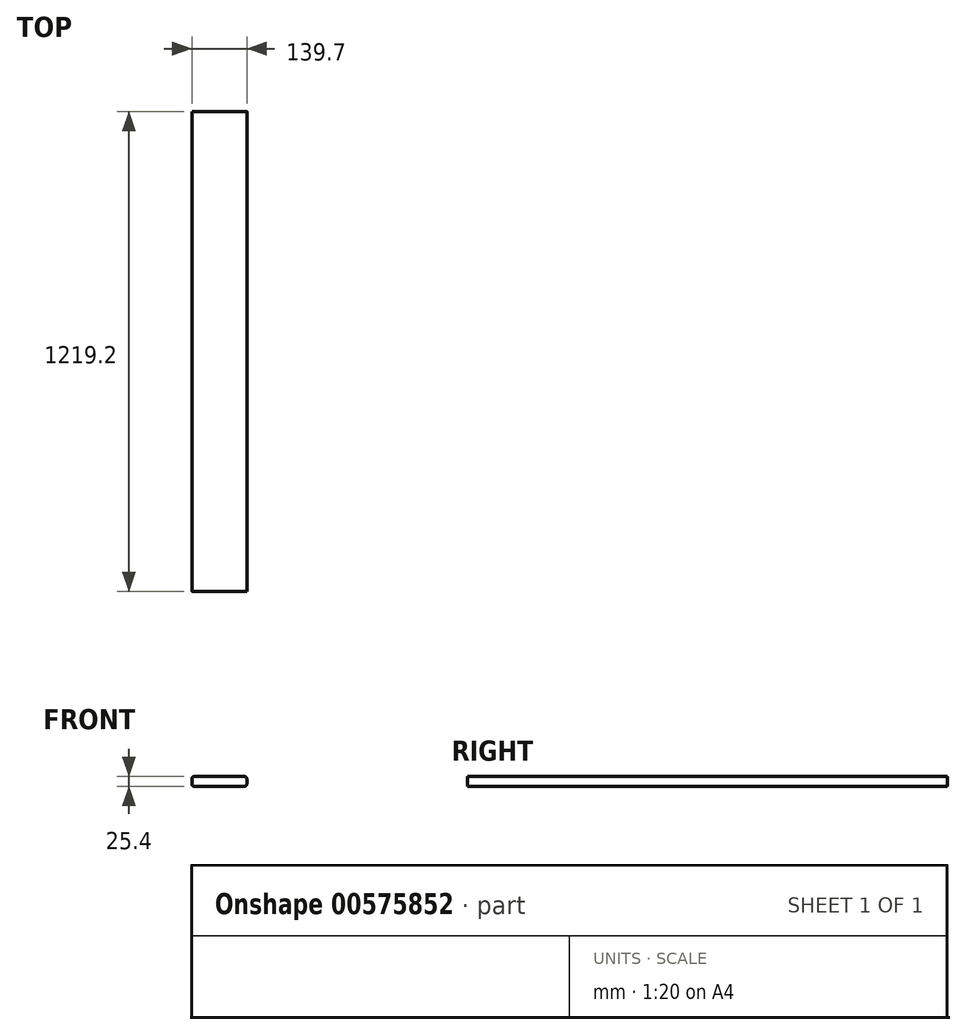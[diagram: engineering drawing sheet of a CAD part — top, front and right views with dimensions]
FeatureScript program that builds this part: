
annotation { "Feature Type Name" : "Feature", "Feature Type Description" : "" }
export const myFeature = defineFeature(function(context is Context, id is Id, definition is map)
    precondition{}
    {
        {
            var Q0;
            Q0=qCreatedBy(makeId("Front.planeOp"),FACE);
            var sketch = newSketch(context, id + "F0", { "sketchPlane" : qUnion([Q0])});
            skLineSegment(sketch, "E0.bottom", {"start": v(6.35, 0) * mm, "end": v(133.35, 0) * mm});
            skLineSegment(sketch, "E0.top", {"start": v(6.35, 25.4) * mm, "end": v(133.35, 25.4) * mm});
            skLineSegment(sketch, "E0.left", {"start": v(0, 6.35) * mm, "end": v(0, 19.05) * mm});
            skLineSegment(sketch, "E0.right", {"start": v(139.7, 6.35) * mm, "end": v(139.7, 19.05) * mm});
            skPoint(sketch, "E1.visualSharp", {"position": v(0, 25.4) * mm});
            skArc(sketch, "E1.filletArc", {"start": v(6.35, 25.4) * mm, "mid": v(1.86, 23.54) * mm, "end": v(0, 19.05) * mm});
            skPoint(sketch, "E2.visualSharp", {"position": v(139.7, 25.4) * mm});
            skArc(sketch, "E2.filletArc", {"start": v(139.7, 19.05) * mm, "mid": v(137.84, 23.54) * mm, "end": v(133.35, 25.4) * mm});
            skPoint(sketch, "E3.visualSharp", {"position": v(139.7, 0) * mm});
            skArc(sketch, "E3.filletArc", {"start": v(133.35, 0) * mm, "mid": v(137.84, 1.86) * mm, "end": v(139.7, 6.35) * mm});
            skPoint(sketch, "E4.visualSharp", {"position": v(0, 0) * mm});
            skArc(sketch, "E4.filletArc", {"start": v(0, 6.35) * mm, "mid": v(1.86, 1.86) * mm, "end": v(6.35, 0) * mm});
            skSolve(sketch);
        }
        {
            var Q0;
            Q0 = qSketchRegion(id + "F0", true);
            extrude(context, id + "F1", {"entities" : qUnion([Q0]), "depth" : 1219.2 * mm, "offsetDistance" : 25.4 * mm});
        }
    });
